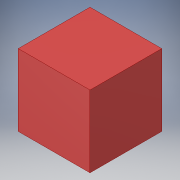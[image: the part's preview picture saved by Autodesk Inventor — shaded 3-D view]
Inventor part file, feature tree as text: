
AUTODESK INVENTOR PART (.ipt)
format: ipt  version: 2019.3 (Build 233278000, 278)  size: 201,216 bytes
history: native  units: mm
features: extrude x1, sketch x1
ambient origin geometry x8: Origin, YZ Plane, XZ Plane, XY Plane, X Axis, Y Axis, Z Axis, Center Point
bodies: Solide1 (feature_tree)
feature tree (2):
  extrude  "Bloc1"  Depth=20.0mm
  sketch  "Esquisse1"
